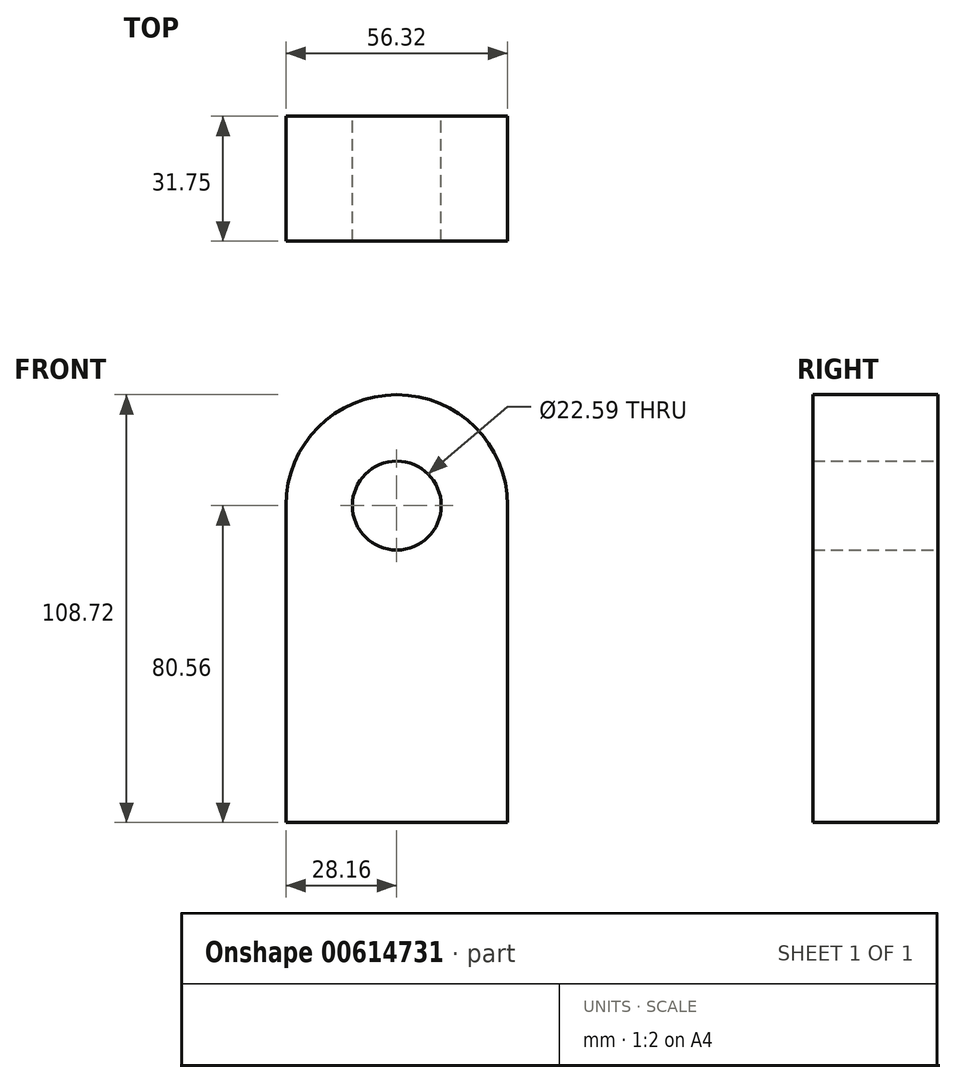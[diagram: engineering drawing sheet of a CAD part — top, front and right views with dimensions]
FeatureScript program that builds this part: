
annotation { "Feature Type Name" : "Feature", "Feature Type Description" : "" }
export const myFeature = defineFeature(function(context is Context, id is Id, definition is map)
    precondition{}
    {
        {
            var Q0;
            Q0=qCreatedBy(makeId("Front.planeOp"),FACE);
            var sketch = newSketch(context, id + "F0", { "sketchPlane" : qUnion([Q0])});
            skLineSegment(sketch, "E0.top", {"start": v(28.16, -40.28) * mm, "end": v(-28.16, -40.28) * mm});
            skLineSegment(sketch, "E0.left", {"start": v(28.16, 40.28) * mm, "end": v(28.16, -40.28) * mm});
            skLineSegment(sketch, "E0.right", {"start": v(-28.16, 40.28) * mm, "end": v(-28.16, -40.28) * mm});
            skPoint(sketch, "E0.middle", {"position": v(0, 0) * mm});
            skArc(sketch, "E1", {"start": v(28.16, 40.28) * mm, "mid": v(0, 68.44) * mm, "end": v(-28.16, 40.28) * mm});
            skCircle(sketch, "E2", {"center": v(0, 40.28) * mm, "radius": 11.3 * mm});
            skSolve(sketch);
        }
        {
            var Q0;
            Q0=makeQuery(id+"F0.imprint","IMPRINT",FACE,{"disambiguationData":[TD([[makeQuery(id+"F0.imprint","IMPRINT",EDGE,{"derivedFrom":sQuery(id+"F0.wireOp",EDGE,"E0.top")}),-1.0]])]});
            extrude(context, id + "F1", {"entities" : qUnion([Q0]), "depth" : 31.75 * mm, "offsetDistance" : 25.4 * mm});
        }
    });
